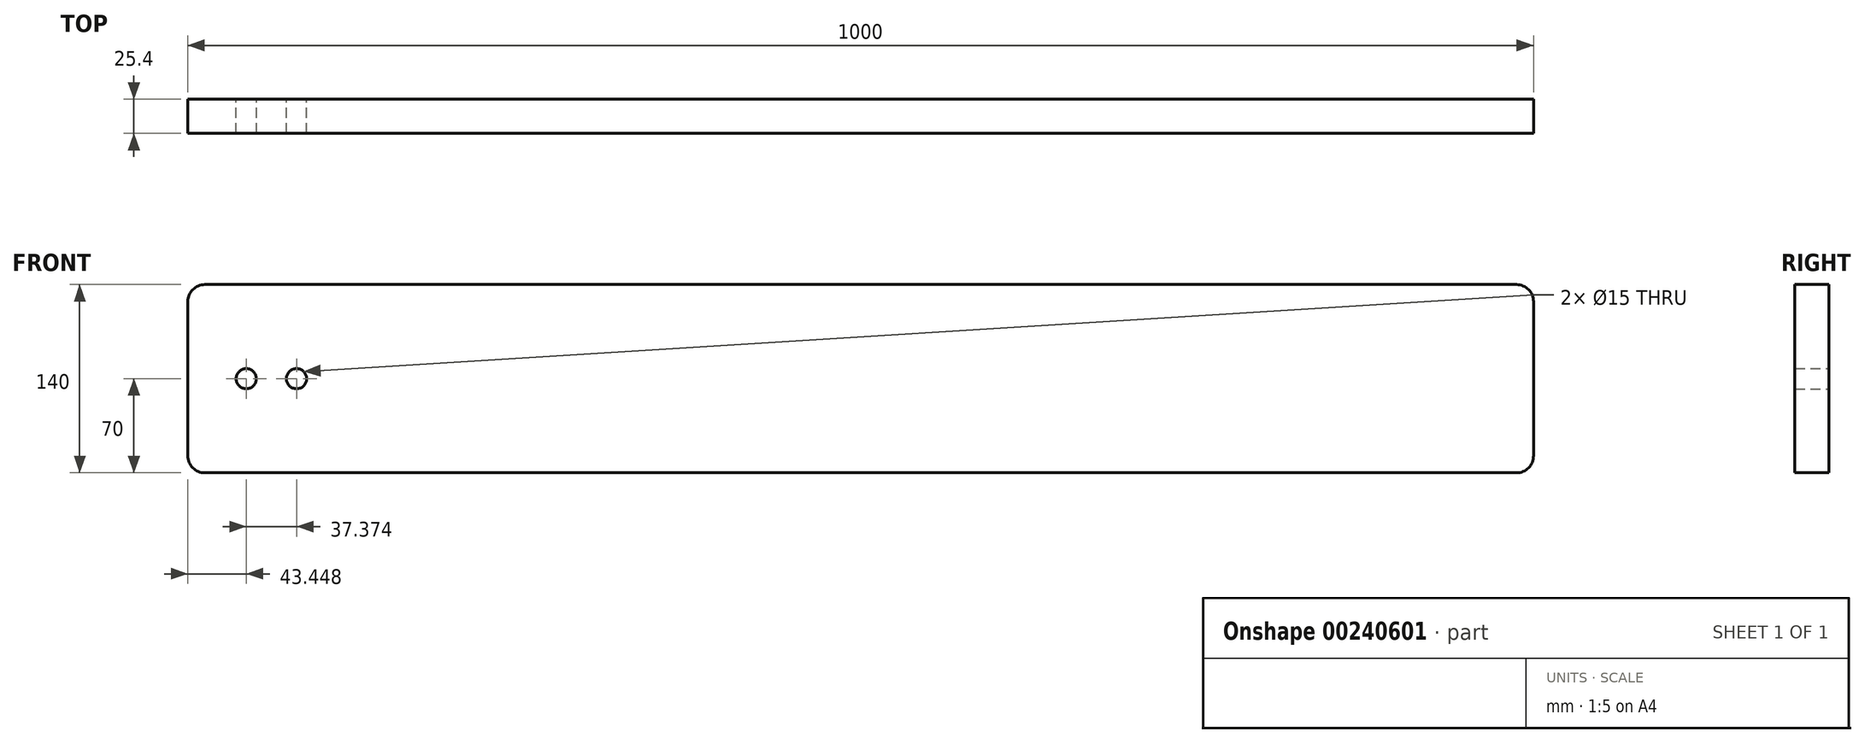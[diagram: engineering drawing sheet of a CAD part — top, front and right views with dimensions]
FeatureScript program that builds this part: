
annotation { "Feature Type Name" : "Feature", "Feature Type Description" : "" }
export const myFeature = defineFeature(function(context is Context, id is Id, definition is map)
    precondition{}
    {
        {
            var Q0;
            Q0=qCreatedBy(makeId("Front.planeOp"),FACE);
            var sketch = newSketch(context, id + "F0", { "sketchPlane" : qUnion([Q0])});
            skLineSegment(sketch, "E0.bottom", {"start": v(500, 70) * mm, "end": v(-500, 70) * mm});
            skLineSegment(sketch, "E0.top", {"start": v(500, -70) * mm, "end": v(-500, -70) * mm});
            skLineSegment(sketch, "E0.left", {"start": v(500, 70) * mm, "end": v(500, -70) * mm});
            skLineSegment(sketch, "E0.right", {"start": v(-500, 70) * mm, "end": v(-500, -70) * mm});
            skPoint(sketch, "E0.middle", {"position": v(0, 0) * mm});
            skCircle(sketch, "E1", {"center": v(-456.55, 0) * mm, "radius": 7.5 * mm});
            skCircle(sketch, "E2", {"center": v(-419.18, 0) * mm, "radius": 7.5 * mm});
            skSolve(sketch);
        }
        {
            var Q0;
            Q0=makeQuery(id+"F0.imprint","IMPRINT",FACE,{"disambiguationData":[TD([[makeQuery(id+"F0.imprint","IMPRINT",EDGE,{"derivedFrom":sQuery(id+"F0.wireOp",EDGE,"E0.bottom")}),1.0]])]});
            extrude(context, id + "F1", {"entities" : qUnion([Q0]), "endBound" : BoundingType.SYMMETRIC, "depth" : 25.4 * mm});
        }
        {
            var Q0;
            Q0=makeQuery(id+"F1.opExtrude","SWEPT_EDGE",EDGE,{"disambiguationData":[OSD([sQuery(id+"F0.wireOp",EDGE,"E0.bottom"),sQuery(id+"F0.wireOp",EDGE,"E0.right")])]});
            var Q1;
            Q1=makeQuery(id+"F1.opExtrude","SWEPT_EDGE",EDGE,{"disambiguationData":[OSD([sQuery(id+"F0.wireOp",EDGE,"E0.top"),sQuery(id+"F0.wireOp",EDGE,"E0.right")])]});
            var Q2;
            Q2=makeQuery(id+"F1.opExtrude","SWEPT_EDGE",EDGE,{"disambiguationData":[OSD([sQuery(id+"F0.wireOp",EDGE,"E0.bottom"),sQuery(id+"F0.wireOp",EDGE,"E0.left")])]});
            var Q3;
            Q3=makeQuery(id+"F1.opExtrude","SWEPT_EDGE",EDGE,{"disambiguationData":[OSD([sQuery(id+"F0.wireOp",EDGE,"E0.top"),sQuery(id+"F0.wireOp",EDGE,"E0.left")])]});
            fillet(context, id + "F2", {"entities" : qUnion([Q0, Q1, Q2, Q3]), "radius" : 12.7 * mm, "tangentPropagation" : true, "allowEdgeOverflow" : false});
        }
    });
